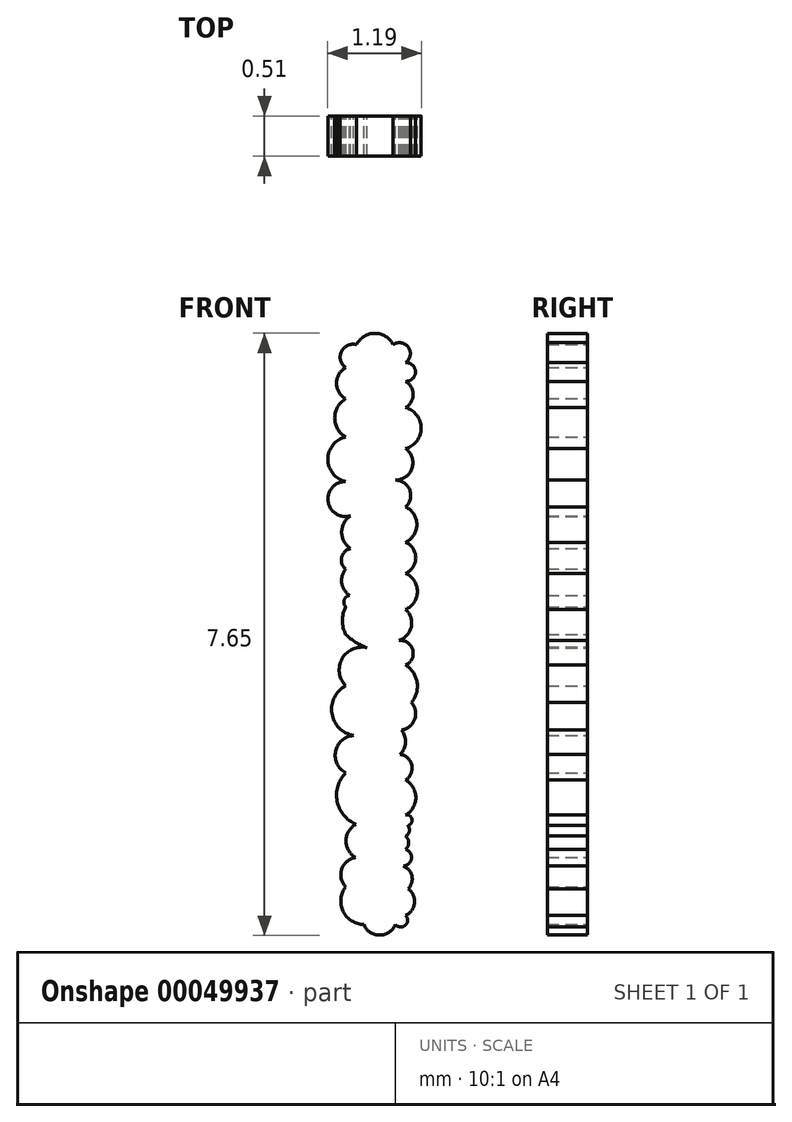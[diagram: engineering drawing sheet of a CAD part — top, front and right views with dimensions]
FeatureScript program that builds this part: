
annotation { "Feature Type Name" : "Feature", "Feature Type Description" : "" }
export const myFeature = defineFeature(function(context is Context, id is Id, definition is map)
    precondition{}
    {
        {
            var Q0;
            Q0=qCreatedBy(makeId("Front.planeOp"),FACE);
            var sketch = newSketch(context, id + "F0", { "sketchPlane" : qUnion([Q0])});
            skLineSegment(sketch, "E0", {"start": v(0, 0) * mm, "end": v(0.76, 0) * mm, "construction": true});
            skLineSegment(sketch, "E1", {"start": v(0, 7.37) * mm, "end": v(0, 0) * mm, "construction": true});
            skLineSegment(sketch, "E2", {"start": v(0, 7.37) * mm, "end": v(0.76, 7.37) * mm, "construction": true});
            skLineSegment(sketch, "E3", {"start": v(0.76, 7.37) * mm, "end": v(0.76, 0) * mm, "construction": true});
            skArc(sketch, "E4", {"start": v(0, 0.48) * mm, "mid": v(-0.03, 0.17) * mm, "end": v(0.23, 0) * mm});
            skArc(sketch, "E5", {"start": v(0.23, 0) * mm, "mid": v(0.43, -0.14) * mm, "end": v(0.63, 0) * mm});
            skArc(sketch, "E6", {"start": v(0.63, 0) * mm, "mid": v(0.76, -0.01) * mm, "end": v(0.76, 0.11) * mm});
            skArc(sketch, "E7", {"start": v(0.76, 0.11) * mm, "mid": v(0.88, 0.3) * mm, "end": v(0.76, 0.47) * mm});
            skArc(sketch, "E8", {"start": v(0.8, 0.45) * mm, "mid": v(0.82, 0.66) * mm, "end": v(0.63, 0.75) * mm});
            skArc(sketch, "E9", {"start": v(0.73, 0.74) * mm, "mid": v(0.83, 0.84) * mm, "end": v(0.76, 0.95) * mm});
            skArc(sketch, "E10", {"start": v(0.76, 0.95) * mm, "mid": v(0.78, 1.1) * mm, "end": v(0.64, 1.14) * mm});
            skArc(sketch, "E11", {"start": v(0.76, 1.12) * mm, "mid": v(0.8, 1.2) * mm, "end": v(0.76, 1.28) * mm});
            skArc(sketch, "E12", {"start": v(0.79, 1.26) * mm, "mid": v(0.84, 1.34) * mm, "end": v(0.76, 1.4) * mm});
            skArc(sketch, "E13", {"start": v(0.76, 1.4) * mm, "mid": v(0.9, 1.61) * mm, "end": v(0.76, 1.83) * mm});
            skArc(sketch, "E14", {"start": v(0.76, 1.83) * mm, "mid": v(0.81, 2.09) * mm, "end": v(0.55, 2.12) * mm});
            skArc(sketch, "E15", {"start": v(0.7, 2.16) * mm, "mid": v(0.76, 2.34) * mm, "end": v(0.66, 2.51) * mm});
            skArc(sketch, "E16", {"start": v(0.7, 2.47) * mm, "mid": v(0.89, 2.65) * mm, "end": v(0.76, 2.87) * mm});
            skArc(sketch, "E17", {"start": v(0.84, 2.82) * mm, "mid": v(0.9, 3.07) * mm, "end": v(0.76, 3.3) * mm});
            skArc(sketch, "E18", {"start": v(0.76, 3.3) * mm, "mid": v(0.82, 3.55) * mm, "end": v(0.56, 3.55) * mm});
            skArc(sketch, "E19", {"start": v(0.68, 3.6) * mm, "mid": v(0.83, 3.78) * mm, "end": v(0.76, 4) * mm});
            skArc(sketch, "E20", {"start": v(0.76, 4) * mm, "mid": v(0.91, 4.23) * mm, "end": v(0.76, 4.46) * mm});
            skArc(sketch, "E21", {"start": v(0.76, 4.46) * mm, "mid": v(0.88, 4.72) * mm, "end": v(0.64, 4.87) * mm});
            skArc(sketch, "E22", {"start": v(0.76, 4.86) * mm, "mid": v(0.9, 5.08) * mm, "end": v(0.76, 5.3) * mm});
            skArc(sketch, "E23", {"start": v(0.76, 5.3) * mm, "mid": v(0.76, 5.6) * mm, "end": v(0.47, 5.55) * mm});
            skArc(sketch, "E24", {"start": v(0.64, 5.64) * mm, "mid": v(0.84, 5.8) * mm, "end": v(0.76, 6.04) * mm});
            skArc(sketch, "E25", {"start": v(0.76, 6.04) * mm, "mid": v(0.96, 6.3) * mm, "end": v(0.76, 6.57) * mm});
            skArc(sketch, "E26", {"start": v(0.76, 6.57) * mm, "mid": v(0.82, 6.84) * mm, "end": v(0.54, 6.89) * mm});
            skArc(sketch, "E27", {"start": v(0.76, 6.9) * mm, "mid": v(0.89, 7.02) * mm, "end": v(0.76, 7.14) * mm});
            skArc(sketch, "E28", {"start": v(0.76, 7.14) * mm, "mid": v(0.8, 7.33) * mm, "end": v(0.6, 7.37) * mm});
            skArc(sketch, "E29", {"start": v(0.6, 7.37) * mm, "mid": v(0.37, 7.5) * mm, "end": v(0.14, 7.37) * mm});
            skArc(sketch, "E30", {"start": v(0.14, 7.37) * mm, "mid": v(-0.05, 7.28) * mm, "end": v(0, 7.07) * mm});
            skArc(sketch, "E31", {"start": v(0, 7.07) * mm, "mid": v(-0.12, 6.88) * mm, "end": v(0, 6.68) * mm});
            skArc(sketch, "E32", {"start": v(0, 6.68) * mm, "mid": v(-0.12, 6.34) * mm, "end": v(0.18, 6.16) * mm});
            skArc(sketch, "E33", {"start": v(0, 6.2) * mm, "mid": v(-0.23, 5.9) * mm, "end": v(0, 5.63) * mm});
            skArc(sketch, "E34", {"start": v(0, 5.63) * mm, "mid": v(-0.18, 5.27) * mm, "end": v(0.2, 5.34) * mm});
            skArc(sketch, "E35", {"start": v(0.12, 5.22) * mm, "mid": v(-0.05, 4.94) * mm, "end": v(0.2, 4.73) * mm});
            skArc(sketch, "E36", {"start": v(0.3, 0.8) * mm, "mid": v(0, 0.78) * mm, "end": v(0, 0.48) * mm});
            skArc(sketch, "E37", {"start": v(0.13, 1.27) * mm, "mid": v(0, 1.06) * mm, "end": v(0.13, 0.85) * mm});
            skArc(sketch, "E38", {"start": v(0, 1.92) * mm, "mid": v(-0.1, 1.56) * mm, "end": v(0.13, 1.27) * mm});
            skArc(sketch, "E39", {"start": v(0.18, 2.4) * mm, "mid": v(-0.12, 2.24) * mm, "end": v(0, 1.92) * mm});
            skArc(sketch, "E40", {"start": v(0, 3.03) * mm, "mid": v(-0.17, 2.64) * mm, "end": v(0.18, 2.4) * mm});
            skArc(sketch, "E41", {"start": v(0.31, 3.5) * mm, "mid": v(-0.03, 3.4) * mm, "end": v(0, 3.03) * mm});
            skArc(sketch, "E42", {"start": v(0, 3.68) * mm, "mid": v(0.14, 3.57) * mm, "end": v(0.31, 3.5) * mm});
            skArc(sketch, "E43", {"start": v(0, 4.04) * mm, "mid": v(-0.04, 3.86) * mm, "end": v(0, 3.68) * mm});
            skArc(sketch, "E44", {"start": v(0.13, 4.15) * mm, "mid": v(0, 4.16) * mm, "end": v(0, 4.04) * mm});
            skArc(sketch, "E45", {"start": v(0, 4.51) * mm, "mid": v(-0.05, 4.34) * mm, "end": v(0.05, 4.18) * mm});
            skArc(sketch, "E46", {"start": v(0.06, 4.78) * mm, "mid": v(-0.05, 4.66) * mm, "end": v(0, 4.51) * mm});
            skSolve(sketch);
        }
        {
            var Q0;
            Q0 = qSketchRegion(id + "F0", true);
            extrude(context, id + "F1", {"entities" : qUnion([Q0]), "depth" : 0.5 * mm});
        }
    });
